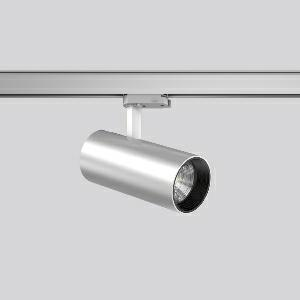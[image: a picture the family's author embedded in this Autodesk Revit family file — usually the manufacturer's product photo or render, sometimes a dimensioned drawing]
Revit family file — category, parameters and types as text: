
# Revit family: deecos_s_mini_742200_004_76_f436
name_source: partatom
category: Lighting Fixtures
units: mm (PartAtom-declared; Revit-internal decimal feet)

## family parameters
Cut with Voids When Loaded = No
Host = Face
Light Source = No
Part Type = Normal
Room Calculation Point = No
Round Connector Dimension = Use Diameter
Shared = No

## types (1)
- DEECOS S mini (1 x LED Modul 930, 2000 lm, 3000)
    Apparent Load = 20 VA
    Approval mark = CE
    CIE Flux Codes = 98 100 100 100 100
    Color Rendering = 90
    Color Temperature = 3000
    Default Elevation = 1800 mm
    Description = Series: DEECOS S mini
LED surface-mounted projector in modern design with no visible cooling ribs. Housing: die-cast aluminium, powder-coated. Rotation range: 356°. Swivel range: 90°. Black plastic ring and recessed LED to prevent glare from the side. Optical assembly with lens made of plastic (polycarbonate) for the best homogeneous light distribution - can be changed without tools. Best colour rendering index Ra>90. With adapter for RZB 3-circuit DALI tracks. Suitable for Track on ceiling, Wall track. High quality converter without flickering and stroboscopic effect. The following accessories can be mounted without use of tools: interchangeable lenses, decorative glasses, honeycomb louvre, clear and frosted diffusers, white interchangeable plastic ring. 
Colour: silver
Diameter: 87 mm
Height: 214 mm
Lamp: LED
Socket: without socket
Colour temperature: 3000K
Colour rendering index (CRI): 92
System power: 20 W
Rated luminous flux: 2000 lm
Luminous efficiency: 100 lm/W
Control gear: Converter, dimmable, DALI
Protection class: I
Type of protection: IP 20
    Height = 214 mm
    Lamp = 1 x LED Modul 930
    Lamp Light Flux = 2000 lm
    Lamp count = 1
    Length = 87 mm
    Lifetime = 50000 h
    Luminous efficacy = 100 lm/W
    Manufacturer = RZB
    ModVariant = No
    Model = 742200.004.76
    Mounting Place = Ceiling
    Mounting Type = Rail mounted
    Number of Poles = 1
    OnlyDefault = Yes
    Power Factor = 1
    Product Name = DEECOS S mini
    Product group = Track mounted projectors
    ProductGroupID = 301
    Protection Class = Protection class I
    Protection Degree = IP 20
    RLX_Detail_Level = 1
    RLX_Emergency_Light_Flux = 0 lm
    RLX_Emergency_Type = 0
    RLX_Emergency_Type_DB = No
    RlxData = <blob elided: 37073 chars, md5=7cad4fca>
    Socket = socket
    Standby Power = 0 W
    System Light Flux = 2000 lm
    System Power = 20 W
    Type Comments = Product without accessories
    Type Image = 741930.004.jpg
    URL = http://relux.com
    VarID = ---
    Voltage = 230 V
    Voltage Range = 220-240 V
    Weight = 0.00 kg
    Width = 0 mm  [stored 0 ft]

note: [stored X ft] marks values corroborated as IEEE doubles in the binary element streams (Revit-internal decimal feet)

## geometry (parser evidence)
native form markers: Blend x4, Sweep x13
no freeform markers — native parametric forms only
